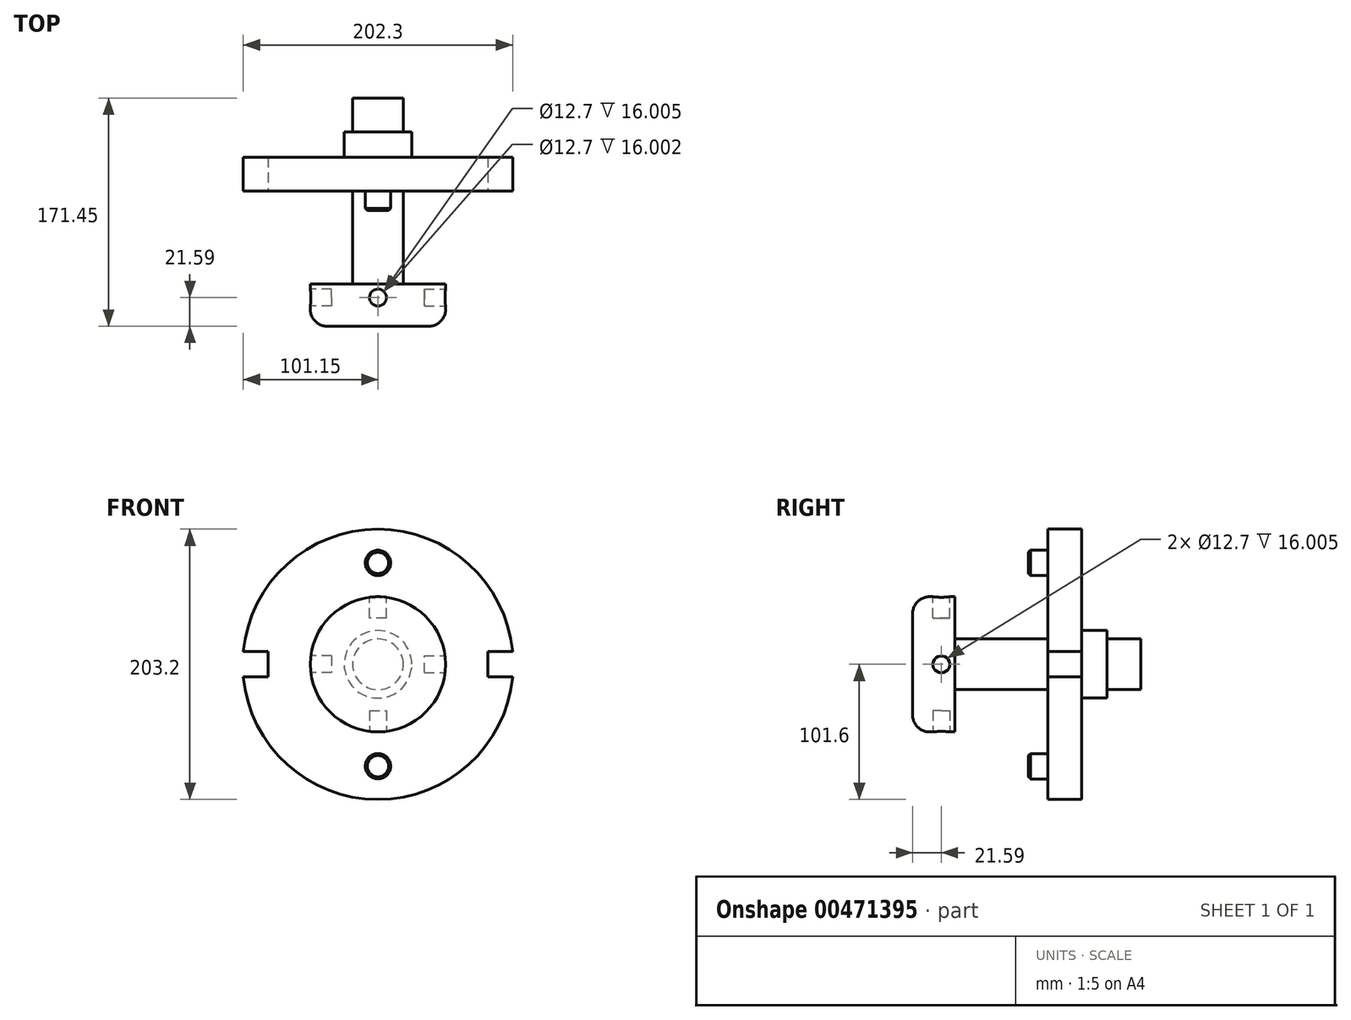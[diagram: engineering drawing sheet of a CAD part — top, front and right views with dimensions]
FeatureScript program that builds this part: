
annotation { "Feature Type Name" : "Feature", "Feature Type Description" : "" }
export const myFeature = defineFeature(function(context is Context, id is Id, definition is map)
    precondition{}
    {
        {
            var Q0;
            Q0=qCreatedBy(makeId("Front.planeOp"),FACE);
            var sketch = newSketch(context, id + "F0", { "sketchPlane" : qUnion([Q0])});
            skCircle(sketch, "E0", {"center": v(0, 0) * mm, "radius": 101.6 * mm});
            skSolve(sketch);
        }
        {
            var Q0;
            Q0 = qSketchRegion(id + "F0", true);
            extrude(context, id + "F1", {"entities" : qUnion([Q0]), "depth" : 19.05 * mm});
        }
        {
            var Q0;
            Q0=makeQuery(id+"F1.opExtrude","CAP_FACE",FACE,{"disambiguationData":[OSD([sQuery(id+"F0.wireOp",EDGE,"E0")])],"isStart":false});
            var sketch = newSketch(context, id + "F2", { "sketchPlane" : qUnion([Q0])});
            skCircle(sketch, "E1", {"center": v(0, 0) * mm, "radius": 19.05 * mm});
            skSolve(sketch);
        }
        {
            var Q0;
            Q0 = qSketchRegion(id + "F2", true);
            var Q1;
            Q1=makeQuery(id+"F2.imprint","IMPRINT",FACE,{"disambiguationData":[TD([[makeQuery(id+"F2.imprint","IMPRINT",EDGE,{"derivedFrom":sQuery(id+"F2.wireOp",EDGE,"E1")}),1.0]])]});
            extrude(context, id + "F3", {"entities" : qUnion([Q0, Q1]), "operationType" : NewBodyOperationType.ADD, "depth" : 76.2 * mm});
        }
        {
            var Q0;
            Q0=makeQuery(id+"F3.opExtrude","CAP_FACE",FACE,{"disambiguationData":[OSD([sQuery(id+"F2.wireOp",EDGE,"E1")])],"isStart":false});
            var sketch = newSketch(context, id + "F4", { "sketchPlane" : qUnion([Q0])});
            skCircle(sketch, "E2", {"center": v(0, 0) * mm, "radius": 50.8 * mm});
            skSolve(sketch);
        }
        {
            var Q0;
            Q0=makeQuery(id+"F4.imprint","IMPRINT",FACE,{"disambiguationData":[TD([[makeQuery(id+"F4.imprint","IMPRINT",EDGE,{"derivedFrom":sQuery(id+"F4.wireOp",EDGE,"E2")}),1.0]])]});
            var Q1;
            Q1=makeQuery(id+"F4.imprint","IMPRINT",FACE,{"disambiguationData":[TD([[makeQuery(id+"F4.imprint","IMPRINT",EDGE,{"derivedFrom":makeQuery(id+"F3.opExtrude","CAP_EDGE",EDGE,{"disambiguationData":[OSD([sQuery(id+"F2.wireOp",EDGE,"E1")])],"isStart":false})}),1.0]])]});
            extrude(context, id + "F5", {"entities" : qUnion([Q0, Q1]), "operationType" : NewBodyOperationType.ADD, "depth" : 31.75 * mm});
        }
        {
            var Q0;
            Q0=makeQuery(id+"F1.opExtrude","CAP_FACE",FACE,{"disambiguationData":[OSD([sQuery(id+"F0.wireOp",EDGE,"E0")])],"isStart":false});
            var sketch = newSketch(context, id + "F6", { "sketchPlane" : qUnion([Q0])});
            skCircle(sketch, "E3", {"center": v(0, 76.2) * mm, "radius": 9.53 * mm});
            skCircle(sketch, "E4", {"center": v(0, -76.58) * mm, "radius": 9.52 * mm});
            skSolve(sketch);
        }
        {
            var Q0;
            Q0 = qSketchRegion(id + "F6", true);
            extrude(context, id + "F7", {"entities" : qUnion([Q0]), "operationType" : NewBodyOperationType.ADD, "depth" : 20.83 * mm});
        }
        {
            var Q0;
            Q0=makeQuery(id+"F5.opExtrude","CAP_EDGE",EDGE,{"disambiguationData":[OSD([sQuery(id+"F4.wireOp",EDGE,"E2")])],"isStart":false});
            fillet(context, id + "F8", {"entities" : qUnion([Q0]), "radius" : 12.7 * mm, "tangentPropagation" : true, "allowEdgeOverflow" : false});
        }
        {
            var Q0;
            Q0=makeQuery(id+"F1.opExtrude","CAP_FACE",FACE,{"disambiguationData":[OSD([sQuery(id+"F0.wireOp",EDGE,"E0")])],"isStart":true});
            var sketch = newSketch(context, id + "F9", { "sketchPlane" : qUnion([Q0])});
            skCircle(sketch, "E5", {"center": v(0, 0) * mm, "radius": 25.4 * mm});
            skSolve(sketch);
        }
        {
            var Q0;
            Q0 = qSketchRegion(id + "F9", true);
            extrude(context, id + "F10", {"entities" : qUnion([Q0]), "operationType" : NewBodyOperationType.ADD, "depth" : 19.05 * mm});
        }
        {
            var Q0;
            Q0=makeQuery(id+"F10.opExtrude","CAP_FACE",FACE,{"disambiguationData":[OSD([sQuery(id+"F9.wireOp",EDGE,"E5")])],"isStart":false});
            var sketch = newSketch(context, id + "F11", { "sketchPlane" : qUnion([Q0])});
            skCircle(sketch, "E6", {"center": v(0, 0) * mm, "radius": 19.05 * mm});
            skSolve(sketch);
        }
        {
            var Q0;
            Q0=makeQuery(id+"F11.imprint","IMPRINT",FACE,{"disambiguationData":[TD([[makeQuery(id+"F11.imprint","IMPRINT",EDGE,{"derivedFrom":sQuery(id+"F11.wireOp",EDGE,"E6")}),1.0]])]});
            extrude(context, id + "F12", {"entities" : qUnion([Q0]), "operationType" : NewBodyOperationType.ADD, "depth" : 25.4 * mm});
        }
        {
            var Q0;
            Q0 = qSketchRegion(id + "F0", true);
            extrude(context, id + "F13", {"entities" : qUnion([Q0]), "operationType" : NewBodyOperationType.ADD, "depth" : 25.4 * mm});
        }
        {
            var Q0;
            Q0=makeQuery(id+"F13.opExtrude","CAP_FACE",FACE,{"disambiguationData":[OSD([sQuery(id+"F0.wireOp",EDGE,"E0")])],"isStart":false});
            var sketch = newSketch(context, id + "F14", { "sketchPlane" : qUnion([Q0])});
            skLineSegment(sketch, "E7", {"start": v(0, 0) * mm, "end": v(82.55, 0) * mm});
            skLineSegment(sketch, "E8", {"start": v(82.55, 0) * mm, "end": v(82.55, 9.53) * mm});
            skLineSegment(sketch, "E9", {"start": v(82.55, 0) * mm, "end": v(82.55, -9.53) * mm});
            skLineSegment(sketch, "E10", {"start": v(82.55, -9.53) * mm, "end": v(120.55, -9.53) * mm});
            skLineSegment(sketch, "E11", {"start": v(120.55, -9.53) * mm, "end": v(120.55, 9.53) * mm});
            skLineSegment(sketch, "E12", {"start": v(120.55, 9.53) * mm, "end": v(82.55, 9.53) * mm});
            skSolve(sketch);
        }
        {
            var Q0;
            {var subQ0=sQuery(id+"F14.wireOp",EDGE,"E11");Q0=makeQuery(id+"F14.imprint","IMPRINT",FACE,{"disambiguationData":[TD([[makeQuery(id+"F14.imprint","IMPRINT",EDGE,{"derivedFrom":subQ0}),1.0]])]});}
            var Q1;
            {var subQ5=sQuery(id+"F14.wireOp",EDGE,"E8");Q1=makeQuery(id+"F14.imprint","IMPRINT",FACE,{"disambiguationData":[TD([[makeQuery(id+"F14.imprint","IMPRINT",EDGE,{"derivedFrom":subQ5}),-1.0]])]});}
            var Q2;
            Q2=sQuery(id+"F14.wireOp",EDGE,"E10");
            var Q3;
            Q3=sQuery(id+"F14.wireOp",EDGE,"E12");
            var Q4;
            Q4=sQuery(id+"F14.wireOp",EDGE,"E9");
            var Q5;
            Q5=sQuery(id+"F14.wireOp",EDGE,"E11");
            var Q6;
            Q6=sQuery(id+"F14.wireOp",EDGE,"E8");
            extrude(context, id + "F15", {"entities" : qUnion([Q0, Q1]), "operationType" : NewBodyOperationType.REMOVE, "surfaceEntities" : qUnion([Q2, Q3, Q4, Q5, Q6]), "oppositeDirection" : true, "depth" : 27.94 * mm});
        }
        {
            var Q0;
            Q0=makeQuery(id+"F13.opExtrude","CAP_FACE",FACE,{"disambiguationData":[OSD([sQuery(id+"F0.wireOp",EDGE,"E0")])],"isStart":false});
            var sketch = newSketch(context, id + "F16", { "sketchPlane" : qUnion([Q0])});
            skLineSegment(sketch, "E13", {"start": v(0, 0) * mm, "end": v(-82.55, 0) * mm});
            skLineSegment(sketch, "E14", {"start": v(-82.55, 0) * mm, "end": v(-82.55, 9.52) * mm});
            skLineSegment(sketch, "E15", {"start": v(-82.55, 0) * mm, "end": v(-82.55, -9.53) * mm});
            skLineSegment(sketch, "E16", {"start": v(-82.55, -9.53) * mm, "end": v(-117.5, -9.53) * mm});
            skLineSegment(sketch, "E17", {"start": v(-117.5, -9.53) * mm, "end": v(-117.5, 9.52) * mm});
            skLineSegment(sketch, "E18", {"start": v(-117.5, 9.52) * mm, "end": v(-82.55, 9.52) * mm});
            skSolve(sketch);
        }
        {
            var Q0;
            {var subQ0=sQuery(id+"F16.wireOp",EDGE,"E17");Q0=makeQuery(id+"F16.imprint","IMPRINT",FACE,{"disambiguationData":[TD([[makeQuery(id+"F16.imprint","IMPRINT",EDGE,{"derivedFrom":subQ0}),-1.0]])]});}
            var Q1;
            {var subQ5=sQuery(id+"F16.wireOp",EDGE,"E14");Q1=makeQuery(id+"F16.imprint","IMPRINT",FACE,{"disambiguationData":[TD([[makeQuery(id+"F16.imprint","IMPRINT",EDGE,{"derivedFrom":subQ5}),1.0]])]});}
            extrude(context, id + "F17", {"entities" : qUnion([Q0, Q1]), "operationType" : NewBodyOperationType.REMOVE, "oppositeDirection" : true, "depth" : 25.4 * mm});
        }
        {
            var Q0;
            Q0=makeQuery(id+"F7.opExtrude","CAP_EDGE",EDGE,{"disambiguationData":[OSD([sQuery(id+"F6.wireOp",EDGE,"E3")])],"isStart":false});
            var Q1;
            Q1=makeQuery(id+"F7.opExtrude","CAP_EDGE",EDGE,{"disambiguationData":[OSD([sQuery(id+"F6.wireOp",EDGE,"E4")])],"isStart":false});
            chamfer(context, id + "F18", {"entities" : qUnion([Q0, Q1]), "chamferType" : ChamferType.OFFSET_ANGLE, "width" : 1.52 * mm, "oppositeDirection" : false, "angle" : 45 * degree, "tangentPropagation" : true});
        }
        {
            var Q0;
            Q0=qCreatedBy(makeId("Top.planeOp"),FACE);
            cPlane(context, id + "F19", {"entities" : qUnion([Q0]), "cplaneType" : CPlaneType.OFFSET, "offset" : 50.8 * mm, "width" : 152.4 * mm, "height" : 152.4 * mm});
        }
        {
            var Q0;
            Q0=qCreatedBy(id+"F19.planeOp",FACE);
            var sketch = newSketch(context, id + "F20", { "sketchPlane" : qUnion([Q0])});
            skCircle(sketch, "E19", {"center": v(0, -105.4) * mm, "radius": 6.35 * mm});
            skSolve(sketch);
        }
        {
            var Q0;
            Q0 = qSketchRegion(id + "F20", true);
            extrude(context, id + "F21", {"entities" : qUnion([Q0]), "operationType" : NewBodyOperationType.REMOVE, "oppositeDirection" : true, "depth" : 16 * mm});
        }
        {
            var Q0;
            Q0=qCreatedBy(id+"F19.planeOp",FACE);
            cPlane(context, id + "F22", {"entities" : qUnion([Q0]), "cplaneType" : CPlaneType.OFFSET, "offset" : 101.6 * mm, "oppositeDirection" : true, "width" : 152.4 * mm, "height" : 152.4 * mm});
        }
        {
            var Q0;
            Q0=qCreatedBy(id+"F22.planeOp",FACE);
            var sketch = newSketch(context, id + "F23", { "sketchPlane" : qUnion([Q0])});
            skLineSegment(sketch, "E20", {"start": v(0, 0) * mm, "end": v(0, -105.4) * mm});
            skCircle(sketch, "E21", {"center": v(0, -105.4) * mm, "radius": 6.35 * mm});
            skSolve(sketch);
        }
        {
            var Q0;
            Q0 = qSketchRegion(id + "F23", true);
            extrude(context, id + "F24", {"entities" : qUnion([Q0]), "operationType" : NewBodyOperationType.REMOVE, "depth" : 16 * mm});
        }
        {
            var Q0;
            Q0=qCreatedBy(makeId("Right.planeOp"),FACE);
            cPlane(context, id + "F25", {"entities" : qUnion([Q0]), "cplaneType" : CPlaneType.OFFSET, "offset" : 50.8 * mm, "width" : 152.4 * mm, "height" : 152.4 * mm});
        }
        {
            var Q0;
            Q0=qCreatedBy(id+"F25.planeOp",FACE);
            var sketch = newSketch(context, id + "F26", { "sketchPlane" : qUnion([Q0])});
            skLineSegment(sketch, "E22", {"start": v(0, 0) * mm, "end": v(-105.41, 0) * mm});
            skCircle(sketch, "E23", {"center": v(-105.41, 0) * mm, "radius": 6.35 * mm});
            skSolve(sketch);
        }
        {
            var Q0;
            Q0 = qSketchRegion(id + "F26", true);
            extrude(context, id + "F27", {"entities" : qUnion([Q0]), "operationType" : NewBodyOperationType.REMOVE, "oppositeDirection" : true, "depth" : 16 * mm});
        }
        {
            var Q0;
            Q0=qCreatedBy(makeId("Right.planeOp"),FACE);
            cPlane(context, id + "F28", {"entities" : qUnion([Q0]), "cplaneType" : CPlaneType.OFFSET, "offset" : 50.8 * mm, "oppositeDirection" : true, "width" : 152.4 * mm, "height" : 152.4 * mm});
        }
        {
            var Q0;
            Q0=qCreatedBy(id+"F28.planeOp",FACE);
            var sketch = newSketch(context, id + "F29", { "sketchPlane" : qUnion([Q0])});
            skLineSegment(sketch, "E24", {"start": v(0, 0) * mm, "end": v(-105.41, 0) * mm});
            skCircle(sketch, "E25", {"center": v(-105.41, 0) * mm, "radius": 6.35 * mm});
            skSolve(sketch);
        }
        {
            var Q0;
            Q0 = qSketchRegion(id + "F29", true);
            extrude(context, id + "F30", {"entities" : qUnion([Q0]), "operationType" : NewBodyOperationType.REMOVE, "depth" : 16 * mm});
        }
    });
